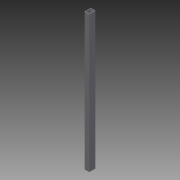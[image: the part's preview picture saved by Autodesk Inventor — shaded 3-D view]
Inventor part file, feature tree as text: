
AUTODESK INVENTOR PART (.ipt)
format: ipt  version: 2013 (Build 170138000, 138)  size: 128,512 bytes
history: native  units: in
note: dims shown in document units (in); Inventor stores cm internally (conversion verified against a paired STEP export)
features: other x3, sketch x1
ambient origin geometry x8: Origin, YZ Plane, XZ Plane, XY Plane, X Axis, Y Axis, Z Axis, Center Point
bodies: Solid1 (feature_tree)
feature tree (4):
  other  "tableFrameSide.ipt"
  other  "Solid1::tableFrameSide.ipt"
  other  "TaggingFeature1"
  sketch  "Sketch2"  dims[d0=0.3937in d20=2.7559in d22=6.0in d27=1.0in d28=0.0in d29=0.1875in d30=4.0in d31=0.75in d4=0.0in d2=0.125in d1=2.0in]
